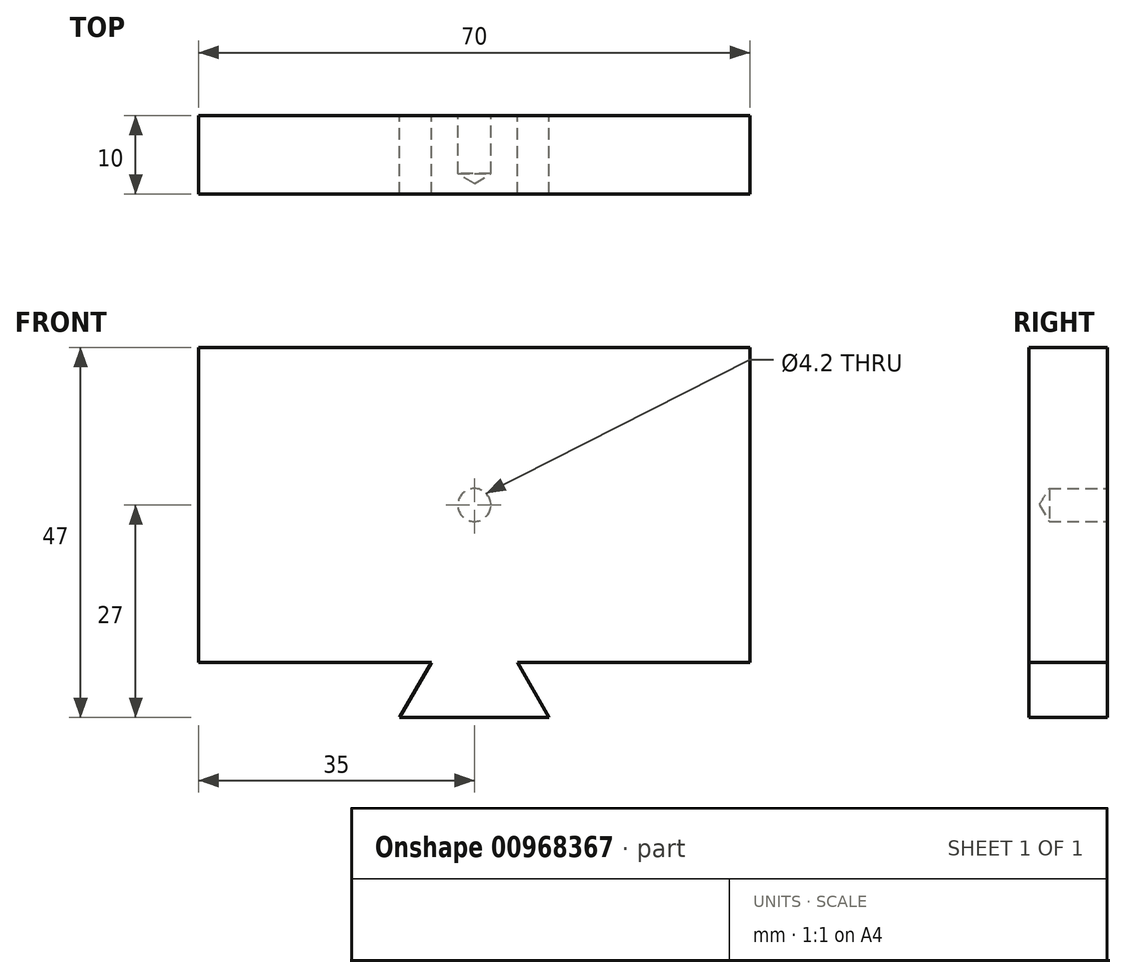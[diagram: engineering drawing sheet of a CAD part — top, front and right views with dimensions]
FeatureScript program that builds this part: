
annotation { "Feature Type Name" : "Feature", "Feature Type Description" : "" }
export const myFeature = defineFeature(function(context is Context, id is Id, definition is map)
    precondition{}
    {
        {
            var Q0;
            Q0=qCreatedBy(makeId("Front.planeOp"),FACE);
            var sketch = newSketch(context, id + "F0", { "sketchPlane" : qUnion([Q0])});
            skLineSegment(sketch, "E0", {"start": v(35, 0) * mm, "end": v(35, 20) * mm});
            skLineSegment(sketch, "E1.bottom", {"start": v(35, 20) * mm, "end": v(-35, 20) * mm});
            skLineSegment(sketch, "E1.top", {"start": v(35, -20) * mm, "end": v(5.46, -20) * mm});
            skLineSegment(sketch, "E1.left", {"start": v(35, 20) * mm, "end": v(35, -20) * mm});
            skLineSegment(sketch, "E1.right", {"start": v(-35, 20) * mm, "end": v(-35, -20) * mm});
            skLineSegment(sketch, "E2", {"start": v(0, -27) * mm, "end": v(9.5, -27) * mm});
            skLineSegment(sketch, "E3", {"start": v(0, -27) * mm, "end": v(-9.5, -27) * mm});
            skLineSegment(sketch, "E4", {"start": v(-9.5, -27) * mm, "end": v(-5.46, -20) * mm});
            skLineSegment(sketch, "E5", {"start": v(9.5, -27) * mm, "end": v(5.46, -20) * mm});
            skLineSegment(sketch, "E6.trimOffspring", {"start": v(-5.46, -20) * mm, "end": v(-35, -20) * mm});
            skPoint(sketch, "E7.start.orphan", {"position": v(0, -20) * mm});
            skPoint(sketch, "E8", {"position": v(0, 0) * mm});
            skSolve(sketch);
        }
        {
            var Q0;
            {var subQ1=sQuery(id+"F0.wireOp",EDGE,"E1.bottom");Q0=makeQuery(id+"F0.imprint","IMPRINT",FACE,{"disambiguationData":[TD([[makeQuery(id+"F0.imprint","IMPRINT",EDGE,{"derivedFrom":subQ1}),1.0]])]});}
            extrude(context, id + "F1", {"entities" : qUnion([Q0]), "depth" : 10 * mm, "offsetDistance" : 25 * mm});
        }
        {
            var Q0;
            Q0=sQuery(id+"F0.wireOp",VERTEX,"E8");
            var Q1;
            Q1=makeQuery(id+"F1.opExtrude","SWEPT_BODY",BODY,{"disambiguationData":[OSD([sQuery(id+"F0.wireOp",EDGE,"E1.bottom"),sQuery(id+"F0.wireOp",EDGE,"E1.top"),sQuery(id+"F0.wireOp",EDGE,"E1.left"),sQuery(id+"F0.wireOp",EDGE,"E1.right"),sQuery(id+"F0.wireOp",EDGE,"E2"),sQuery(id+"F0.wireOp",EDGE,"E3"),sQuery(id+"F0.wireOp",EDGE,"E4"),sQuery(id+"F0.wireOp",EDGE,"E5"),sQuery(id+"F0.wireOp",EDGE,"E6.trimOffspring")])]});
            hole(context, id + "F2", {"style" : HoleStyle.SIMPLE, "endStyle" : HoleEndStyle.BLIND, "oppositeDirection" : true, "standardTappedOrClearance" : lookupTablePath({ "standard" : "ISO", "engagement" : "75%", "pitch" : "0.8 mm", "size" : "M5", "type" : "Tapped" }), "standardBlindInLast" : lookupTablePath({ "standard" : "ISO", "fit" : "Normal", "engagement" : "75%", "pitch" : "0.8 mm", "size" : "M5", "type" : "Clearance & tapped" }), "holeDiameter" : 4.2 * mm, "majorDiameter" : 5 * mm, "showTappedDepth" : true, "holeDepth" : 7.4 * mm, "tappedDepth" : 5 * mm, "tapClearance" : 3, "startFromSketch" : true, "locations" : qUnion([Q0]), "scope" : qUnion([Q1])});
        }
    });
